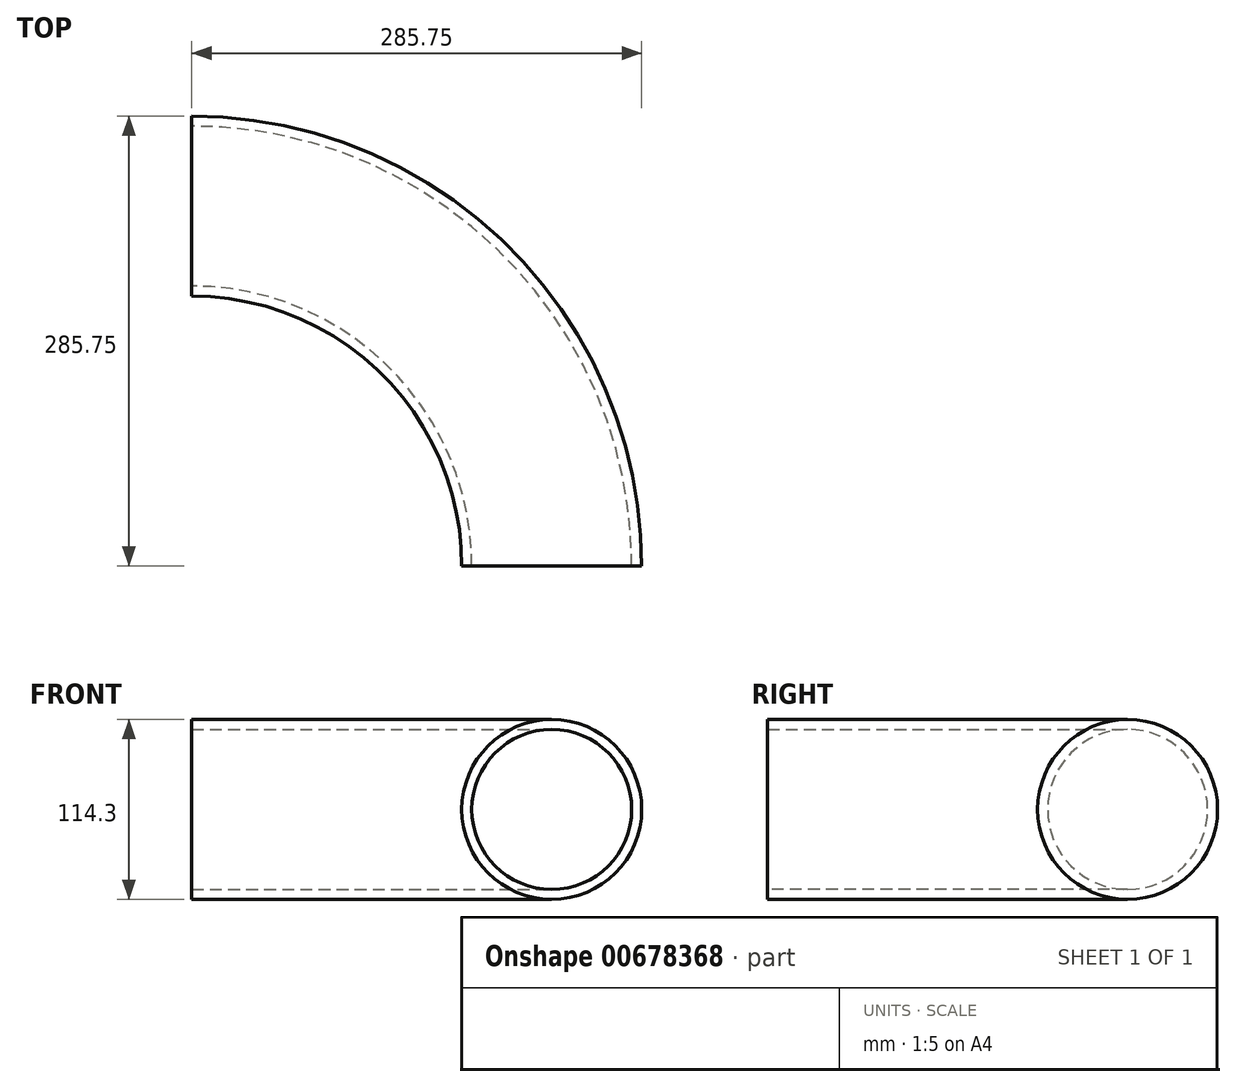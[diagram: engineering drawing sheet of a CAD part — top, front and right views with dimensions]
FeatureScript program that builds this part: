
annotation { "Feature Type Name" : "Feature", "Feature Type Description" : "" }
export const myFeature = defineFeature(function(context is Context, id is Id, definition is map)
    precondition{}
    {
        {
            var Q0;
            Q0=qCreatedBy(makeId("Top.planeOp"),FACE);
            var sketch = newSketch(context, id + "F0", { "sketchPlane" : qUnion([Q0])});
            skArc(sketch, "E0", {"start": v(228.6, 0) * mm, "mid": v(161.64, 161.64) * mm, "end": v(0, 228.6) * mm});
            skSolve(sketch);
        }
        {
            var Q0;
            Q0=qCreatedBy(makeId("Right.planeOp"),FACE);
            var sketch = newSketch(context, id + "F1", { "sketchPlane" : qUnion([Q0])});
            skCircle(sketch, "E1", {"center": v(228.6, 0) * mm, "radius": 57.15 * mm});
            skCircle(sketch, "E2", {"center": v(228.6, 0) * mm, "radius": 50.8 * mm});
            skSolve(sketch);
        }
        {
            var Q0;
            Q0=makeQuery(id+"F1.imprint","IMPRINT",FACE,{"disambiguationData":[TD([[makeQuery(id+"F1.imprint","IMPRINT",EDGE,{"derivedFrom":sQuery(id+"F1.wireOp",EDGE,"E1")}),1.0]])]});
            var Q1;
            Q1=sQuery(id+"F0.wireOp",EDGE,"E0");
            sweep(context, id + "F2", {"profiles" : qUnion([Q0]), "path" : qUnion([Q1])});
        }
    });
